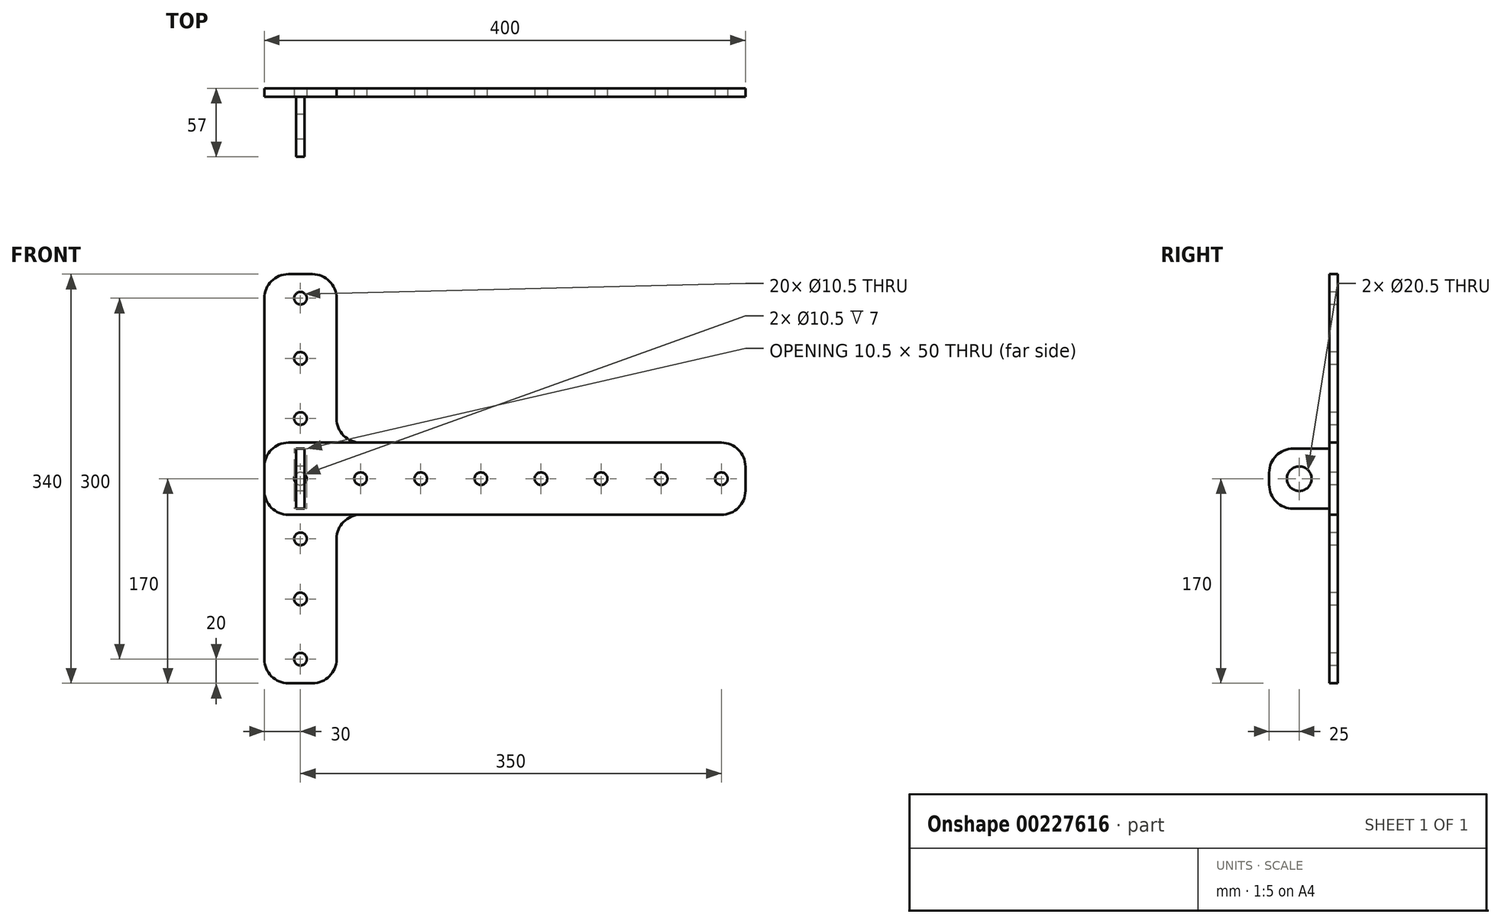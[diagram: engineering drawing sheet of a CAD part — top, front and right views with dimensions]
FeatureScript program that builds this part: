
annotation { "Feature Type Name" : "Feature", "Feature Type Description" : "" }
export const myFeature = defineFeature(function(context is Context, id is Id, definition is map)
    precondition{}
    {
        {
            var Q0;
            Q0=qCreatedBy(makeId("Front.planeOp"),FACE);
            var sketch = newSketch(context, id + "F0", { "sketchPlane" : qUnion([Q0])});
            skLineSegment(sketch, "E0", {"start": v(370, 30) * mm, "end": v(370, -30) * mm});
            skLineSegment(sketch, "E1", {"start": v(370, -30) * mm, "end": v(30, -30) * mm});
            skLineSegment(sketch, "E2", {"start": v(30, -30) * mm, "end": v(30, -170) * mm});
            skLineSegment(sketch, "E3", {"start": v(30, -170) * mm, "end": v(-30, -170) * mm});
            skLineSegment(sketch, "E4", {"start": v(-30, -170) * mm, "end": v(-30, 30) * mm});
            skLineSegment(sketch, "E5", {"start": v(0, 128.1) * mm, "end": v(0, -190.96) * mm, "construction": true});
            skLineSegment(sketch, "E6", {"start": v(-150.27, 0) * mm, "end": v(414.2, 0) * mm, "construction": true});
            skLineSegment(sketch, "E7", {"start": v(-30, 30) * mm, "end": v(370, 30) * mm});
            skCircle(sketch, "E8", {"center": v(50, 0) * mm, "radius": 5.25 * mm});
            skCircle(sketch, "E9", {"center": v(0, -50) * mm, "radius": 5.25 * mm});
            skCircle(sketch, "E10.1.0.0", {"center": v(100, 0) * mm, "radius": 5.25 * mm});
            skCircle(sketch, "E10.2.0.0", {"center": v(150, 0) * mm, "radius": 5.25 * mm});
            skCircle(sketch, "E10.3.0.0", {"center": v(200, 0) * mm, "radius": 5.25 * mm});
            skCircle(sketch, "E10.4.0.0", {"center": v(250, 0) * mm, "radius": 5.25 * mm});
            skCircle(sketch, "E10.5.0.0", {"center": v(300, 0) * mm, "radius": 5.25 * mm});
            skCircle(sketch, "E10.6.0.0", {"center": v(350, 0) * mm, "radius": 5.25 * mm});
            skLineSegment(sketch, "E10.direction1", {"start": v(50, 0) * mm, "end": v(100, 0) * mm, "construction": true});
            skCircle(sketch, "E11", {"center": v(0, -100) * mm, "radius": 5.25 * mm});
            skCircle(sketch, "E12", {"center": v(0, -150) * mm, "radius": 5.25 * mm});
            skCircle(sketch, "E13", {"center": v(0, 0) * mm, "radius": 5.25 * mm});
            skSolve(sketch);
        }
        {
            var Q0;
            Q0 = qSketchRegion(id + "F0", true);
            extrude(context, id + "F1", {"entities" : qUnion([Q0]), "oppositeDirection" : true, "depth" : 7 * mm});
        }
        {
            var Q0;
            Q0=qCreatedBy(makeId("Right.planeOp"),FACE);
            var sketch = newSketch(context, id + "F2", { "sketchPlane" : qUnion([Q0])});
            skLineSegment(sketch, "E14", {"start": v(0, 0) * mm, "end": v(-50, 0) * mm, "construction": true});
            skLineSegment(sketch, "E15", {"start": v(0, 34.39) * mm, "end": v(0, -27.95) * mm, "construction": true});
            skLineSegment(sketch, "E16", {"start": v(0, 25) * mm, "end": v(-50, 25) * mm});
            skLineSegment(sketch, "E17", {"start": v(-50, 25) * mm, "end": v(-50, -25) * mm});
            skLineSegment(sketch, "E18", {"start": v(-50, -25) * mm, "end": v(0, -25) * mm});
            skLineSegment(sketch, "E19", {"start": v(0, -25) * mm, "end": v(0, 25) * mm});
            skCircle(sketch, "E20", {"center": v(-25, 0) * mm, "radius": 10.25 * mm});
            skLineSegment(sketch, "E21", {"start": v(0, 25) * mm, "end": v(-50, -25) * mm, "construction": true});
            skSolve(sketch);
        }
        {
            var Q0;
            Q0=makeQuery(id+"F2.imprint","IMPRINT",FACE,{"disambiguationData":[TD([[makeQuery(id+"F2.imprint","IMPRINT",EDGE,{"derivedFrom":sQuery(id+"F2.wireOp",EDGE,"E16")}),1.0]])]});
            extrude(context, id + "F3", {"entities" : qUnion([Q0]), "operationType" : NewBodyOperationType.ADD, "endBound" : BoundingType.SYMMETRIC, "depth" : 7 * mm});
        }
        {
            var Q0;
            Q0=makeQuery(id+"F3.opExtrude","SWEPT_EDGE",EDGE,{"disambiguationData":[OSD([sQuery(id+"F2.wireOp",EDGE,"E16"),sQuery(id+"F2.wireOp",EDGE,"E17")])]});
            var Q1;
            Q1=makeQuery(id+"F3.opExtrude","SWEPT_EDGE",EDGE,{"disambiguationData":[OSD([sQuery(id+"F2.wireOp",EDGE,"E17"),sQuery(id+"F2.wireOp",EDGE,"E18")])]});
            var Q2;
            Q2=makeQuery(id+"F1.opExtrude","SWEPT_EDGE",EDGE,{"disambiguationData":[OSD([sQuery(id+"F0.wireOp",EDGE,"E0"),sQuery(id+"F0.wireOp",EDGE,"E7")])]});
            var Q3;
            Q3=makeQuery(id+"F1.opExtrude","SWEPT_EDGE",EDGE,{"disambiguationData":[OSD([sQuery(id+"F0.wireOp",EDGE,"E0"),sQuery(id+"F0.wireOp",EDGE,"E1")])]});
            var Q4;
            Q4=makeQuery(id+"F1.opExtrude","SWEPT_EDGE",EDGE,{"disambiguationData":[OSD([sQuery(id+"F0.wireOp",EDGE,"E2"),sQuery(id+"F0.wireOp",EDGE,"E3")])]});
            var Q5;
            Q5=makeQuery(id+"F1.opExtrude","SWEPT_EDGE",EDGE,{"disambiguationData":[OSD([sQuery(id+"F0.wireOp",EDGE,"E3"),sQuery(id+"F0.wireOp",EDGE,"E4")])]});
            var Q6;
            Q6=makeQuery(id+"F1.opExtrude","SWEPT_EDGE",EDGE,{"disambiguationData":[OSD([sQuery(id+"F0.wireOp",EDGE,"E4"),sQuery(id+"F0.wireOp",EDGE,"E7")])]});
            var Q7;
            Q7=makeQuery(id+"F1.opExtrude","SWEPT_EDGE",EDGE,{"disambiguationData":[OSD([sQuery(id+"F0.wireOp",EDGE,"E1"),sQuery(id+"F0.wireOp",EDGE,"E2")])]});
            fillet(context, id + "F4", {"entities" : qUnion([Q0, Q1, Q2, Q3, Q4, Q5, Q6, Q7]), "radius" : 20 * mm, "tangentPropagation" : true, "allowEdgeOverflow" : false});
        }
        {
            var Q0;
            Q0=makeQuery(id+"F1.opExtrude","SWEPT_BODY",BODY,{"disambiguationData":[OSD([sQuery(id+"F0.wireOp",EDGE,"E0"),sQuery(id+"F0.wireOp",EDGE,"E1"),sQuery(id+"F0.wireOp",EDGE,"E2"),sQuery(id+"F0.wireOp",EDGE,"E3"),sQuery(id+"F0.wireOp",EDGE,"E4"),sQuery(id+"F0.wireOp",EDGE,"E7"),sQuery(id+"F0.wireOp",EDGE,"E8"),sQuery(id+"F0.wireOp",EDGE,"E9"),sQuery(id+"F0.wireOp",EDGE,"E10.1.0.0"),sQuery(id+"F0.wireOp",EDGE,"E10.2.0.0"),sQuery(id+"F0.wireOp",EDGE,"E10.3.0.0"),sQuery(id+"F0.wireOp",EDGE,"E10.4.0.0"),sQuery(id+"F0.wireOp",EDGE,"E10.5.0.0"),sQuery(id+"F0.wireOp",EDGE,"E10.6.0.0"),sQuery(id+"F0.wireOp",EDGE,"E11"),sQuery(id+"F0.wireOp",EDGE,"E12"),sQuery(id+"F0.wireOp",EDGE,"E13")])]});
            var Q1;
            Q1=qCreatedBy(makeId("Top.planeOp"),FACE);
            mirror(context, id + "F5", {"entities" : qUnion([Q0]), "mirrorPlane" : qUnion([Q1])});
        }
    });
